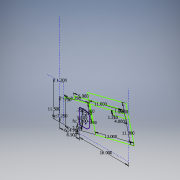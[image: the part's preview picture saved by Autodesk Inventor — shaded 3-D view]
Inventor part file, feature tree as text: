
AUTODESK INVENTOR PART (.ipt)
format: ipt  version: 2017 SP1 (Build 210196100, 196)  size: 124,928 bytes
history: native  units: in
note: dims shown in document units (in); Inventor stores cm internally (conversion verified against a paired STEP export)
features: sketch x1
ambient origin geometry x8: Origin, YZ Plane, XZ Plane, XY Plane, X Axis, Y Axis, Z Axis, Center Point
feature tree (1):
  sketch  "Sketch1"  dims[d0=2.5in d1=5.0in d2=1.25in d3=0.75in d4=16.0in d7=5.0in d8=8.0in d9=5.0in d10=8.25in d11=0.25in d12=13.0in d13=11.0in d14=3.0in d17=3.5in d19=2.0in d20=11.0in d22=1.25in d23=4.0in d24=1.0in d25=6.5in d30=1.0in d31=4.5in d34=11.5in d36=1.0in d38=1.2in d39=1.0in d41=6.5in d42=5.0in d43=0.75in d44=7.25in d45=4.75in]
